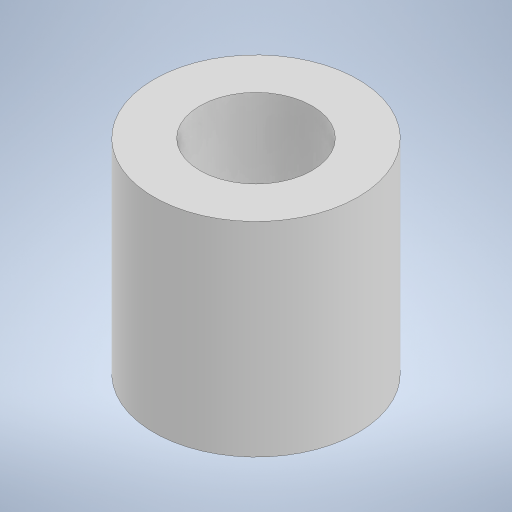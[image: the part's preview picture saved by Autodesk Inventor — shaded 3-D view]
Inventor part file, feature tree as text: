
AUTODESK INVENTOR PART (.ipt)
format: ipt  version: 2023 (Build 270158000, 158)  size: 193,024 bytes
history: native  units: mm
features: extrude x1, sketch x1
ambient origin geometry x8: Origin, YZ Plane, XZ Plane, XY Plane, X Axis, Y Axis, Z Axis, Center Point
bodies: Solid1 (feature_tree)
feature tree (2):
  extrude  "Extrusion1"  Depth=8.0mm
  sketch  "Sketch1"  dims[d0=4.4mm d1=8.0mm d2=8.0mm d3=0.0mm]
